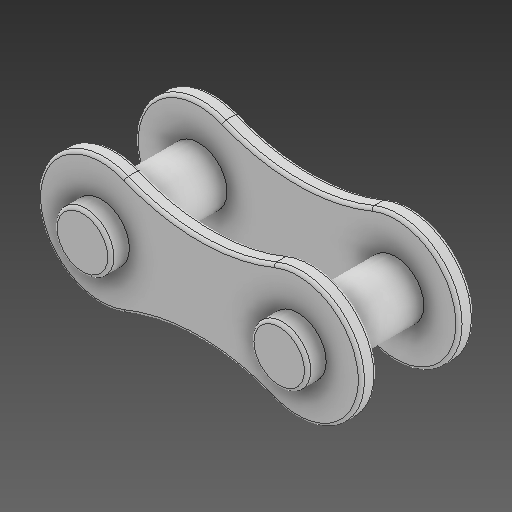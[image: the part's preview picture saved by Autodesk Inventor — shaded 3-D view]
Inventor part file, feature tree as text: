
AUTODESK INVENTOR PART (.ipt)
format: ipt  version: 2021 (Build 250183000, 183)  size: 368,640 bytes
history: native  units: in
note: dims shown in document units (in); Inventor stores cm internally (conversion verified against a paired STEP export)
features: other x4, extrude x2, mirror x2, sketch x2, fillet x1
ambient origin geometry x8: Origin, YZ Plane, XZ Plane, XY Plane, X Axis, Y Axis, Z Axis, Center Point
bodies: Solid1 (feature_tree)
feature tree (11):
  other  "Eslabón 1.ipt"
  extrude  "Extrusion1"  Depth=0.0394in
  mirror  "Mirror1"
  extrude  "Extrusion2"  Depth=0.3819in
  mirror  "Mirror2"
  fillet  "Fillet1"  [1 undecoded]
  other  "TaggingFeature1"
  sketch  "Sketch1"  dims[d0=0.3937in d3=0.0394in]
  sketch  "Sketch2"  dims[d4=0.0in d5=0.3819in d6=0.0in d7=0.0079in]
  other  "Solid1::Eslabón 1.ipt"
  other  "Srf1"
note: 1 required parameter value undecoded (feature->parameter linkage not recoverable at this tier; creation-order binding heuristic only, values carry confidence <= 0.55)
